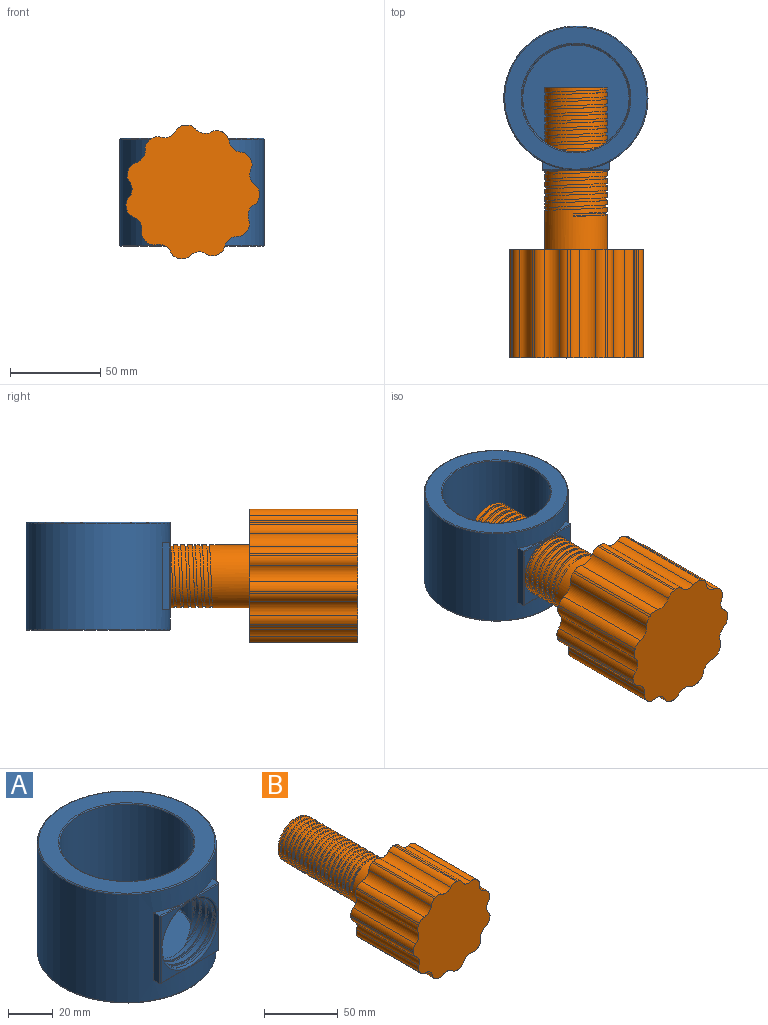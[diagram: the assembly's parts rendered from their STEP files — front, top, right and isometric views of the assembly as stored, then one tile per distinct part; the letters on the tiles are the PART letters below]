
ASSEMBLY  parts=2 mates=1
PART A: 45 faces, bbox 86.7x86.7x60.1 mm
  f0: plane 36.14x18.64mm, normal (0,-1,0), area 141.5mm2, adj f1,f39,f40,f41,f42,f43,f44
  f1: bspline ~6.95x0.63mm, area 1.6mm2, adj f0,f2,f39
  f2: cylinder r=40mm len=80mm, axis (0,0,-1), area 13405.1mm2, adj f1,f3,f4,f5,f6,f10,f11,f12
  f3: plane 12.2x4.04mm, normal (0,0,-1), area 20.2mm2, adj f2,f13,f39
  f4: plane 12.2x4.04mm, normal (0,0,-1), area 20.2mm2, adj f2,f5,f43
  f5: plane 37x4.04mm, normal (1,0,0), area 149.3mm2, adj f2,f4,f6,f42
  f6: plane 12.2x4.04mm, normal (0,0,1), area 20.2mm2, adj f2,f5,f7
  f7: cylinder r=0.5mm len=12.2mm, axis (-1,0,0), area 9.4mm2, adj f6,f8,f10,f42
  f8: plane 36.14x18.64mm, normal (0,-1,0), area 141.5mm2, adj f7,f9,f10,f11,f40,f41,f42
  f9: cylinder r=0.5mm len=12.2mm, axis (-1,0,0), area 9.4mm2, adj f8,f11,f12,f40
  f10: bspline ~6.95x0.63mm, area 1.6mm2, adj f2,f7,f8
  f11: bspline ~6.95x0.63mm, area 1.6mm2, adj f2,f8,f9
  f12: plane 12.2x4.04mm, normal (0,0,1), area 20.2mm2, adj f2,f9,f13
  f13: plane 37x4.04mm, normal (-1,0,0), area 149.3mm2, adj f2,f3,f12,f40
  f14: torus R=39.5mm, axis (0,0,1), area 196.5mm2, adj f2,f15
  f15: plane 79x79mm, normal (0,0,1), area 1979.2mm2, adj f14,f16
  f16: torus R=30.5mm, axis (0,0,1), area 148.9mm2, adj f15,f17
  f17: cylinder r=30mm len=60mm, axis (0,0,1), area 8262.7mm2, adj f16,f18,f20,f21,f22,f23,f24,f25
  f18: bspline ~40.99x35.5mm, area 184.4mm2, adj f17,f19,f24,f26
  f19: plane 0.97x0.75mm, normal (0,0,1), area 0.5mm2, adj f18,f26,f41
  f20: cylinder r=17mm len=21.91mm, axis (0,-1,0), area 35mm2, adj f17,f21
  f21: bspline ~30.74x9.25mm, area 19mm2, adj f17,f20,f22
  f22: cylinder r=17.75mm len=30.4mm, axis (0,-1,0), area 47.6mm2, adj f17,f21,f23
  f23: bspline ~35.87x26.63mm, area 26.9mm2, adj f17,f22,f24
  f24: cylinder r=17mm len=34mm, axis (0,-1,0), area 665.8mm2, adj f17,f18,f23,f25,f41
  f25: bspline ~40.99x35.5mm, area 201.3mm2, adj f17,f24,f26,f41
  f26: cylinder r=17.75mm len=35.5mm, axis (0,-1,0), area 443.9mm2, adj f17,f18,f19,f25,f27,f41
  f27: bspline ~35.87x26.63mm, area 31.5mm2, adj f17,f26,f28
  f28: cylinder r=17mm len=30.79mm, axis (0,-1,0), area 76.4mm2, adj f17,f27,f29
  f29: bspline ~30.74x9.25mm, area 16.6mm2, adj f17,f28,f30
  f30: cylinder r=17.75mm len=21.82mm, axis (0,-1,0), area 27.5mm2, adj f17,f29,f32
  f31: cylinder r=17mm len=7.73mm, axis (0,-1,0), area 0mm2, adj f17,f32
  f32: bspline ~30.74x9.25mm, area 7.8mm2, adj f17,f30,f31
  f33: bspline ~30.74x9.25mm, area 0mm2, adj f17,f34
  f34: cylinder r=17.75mm len=8.04mm, axis (0,-1,0), area 0mm2, adj f17,f33
  f35: torus R=29.5mm, axis (0,0,1), area 147.1mm2, adj f17,f36
  f36: plane 59x59mm, normal (0,0,1), area 2734mm2, adj f35
  f37: torus R=39.5mm, axis (0,0,1), area 196.5mm2, adj f2,f38
  f38: plane 79x79mm, normal (0,0,-1), area 4901.7mm2, adj f37
  f39: cylinder r=0.5mm len=12.2mm, axis (1,0,0), area 9.4mm2, adj f0,f1,f3,f40
  f40: cylinder r=0.5mm len=37mm, axis (0,0,-1), area 28.7mm2, adj f0,f8,f9,f13,f39
  f41: torus R=18mm, axis (0,-1,0), area 138.2mm2, adj f0,f8,f19,f24,f25,f26
  f42: cylinder r=0.5mm len=37mm, axis (0,0,1), area 28.7mm2, adj f0,f5,f7,f8,f43
  f43: cylinder r=0.5mm len=12.2mm, axis (1,0,0), area 9.4mm2, adj f0,f4,f42,f44
  f44: bspline ~6.95x0.63mm, area 1.6mm2, adj f0,f2,f43
PART B: 76 faces, bbox 73.9x150x74.3 mm
  f0: cylinder r=37.43mm len=60mm, axis (0,-1,0), area 76.3mm2, adj f1,f41,f72,f74
  f1: cylinder r=6mm len=60mm, axis (0,1,0), area 347.5mm2, adj f0,f3,f41,f72
  f2: cylinder r=6mm len=60mm, axis (0,1,0), area 347.5mm2, adj f3,f4,f41,f72
  f3: cylinder r=7mm len=60mm, axis (0,-1,0), area 585.2mm2, adj f1,f2,f41,f72
  f4: cylinder r=37.43mm len=60mm, axis (0,-1,0), area 76.3mm2, adj f2,f5,f41,f72
  f5: cylinder r=6mm len=60mm, axis (0,1,0), area 347.5mm2, adj f4,f7,f41,f72
  f6: cylinder r=6mm len=60mm, axis (0,1,0), area 347.5mm2, adj f7,f8,f41,f72
  f7: cylinder r=7mm len=60mm, axis (0,-1,0), area 585.2mm2, adj f5,f6,f41,f72
  f8: cylinder r=37.43mm len=60mm, axis (0,-1,0), area 76.3mm2, adj f6,f9,f41,f72
  f9: cylinder r=6mm len=60mm, axis (0,1,0), area 347.5mm2, adj f8,f11,f41,f72
  f10: cylinder r=6mm len=60mm, axis (0,1,0), area 347.5mm2, adj f11,f12,f41,f72
  f11: cylinder r=7mm len=60mm, axis (0,-1,0), area 585.2mm2, adj f9,f10,f41,f72
  f12: cylinder r=37.43mm len=60mm, axis (0,-1,0), area 76.3mm2, adj f10,f13,f41,f72
  f13: cylinder r=6mm len=60mm, axis (0,1,0), area 347.5mm2, adj f12,f15,f41,f72
  f14: cylinder r=6mm len=60mm, axis (0,1,0), area 347.5mm2, adj f15,f16,f41,f72
  f15: cylinder r=7mm len=60mm, axis (0,-1,0), area 585.2mm2, adj f13,f14,f41,f72
  f16: cylinder r=37.43mm len=60mm, axis (0,-1,0), area 76.3mm2, adj f14,f17,f41,f72
  f17: cylinder r=6mm len=60mm, axis (0,1,0), area 347.5mm2, adj f16,f19,f41,f72
  f18: cylinder r=6mm len=60mm, axis (0,1,0), area 347.5mm2, adj f19,f20,f41,f72
  f19: cylinder r=7mm len=60mm, axis (0,-1,0), area 585.2mm2, adj f17,f18,f41,f72
  f20: cylinder r=37.43mm len=60mm, axis (0,-1,0), area 76.3mm2, adj f18,f21,f41,f72
  f21: cylinder r=6mm len=60mm, axis (0,1,0), area 347.5mm2, adj f20,f23,f41,f72
  f22: cylinder r=6mm len=60mm, axis (0,1,0), area 347.5mm2, adj f23,f24,f41,f72
  f23: cylinder r=7mm len=60mm, axis (0,-1,0), area 585.2mm2, adj f21,f22,f41,f72
  f24: cylinder r=37.43mm len=60mm, axis (0,-1,0), area 76.3mm2, adj f22,f25,f41,f72
  f25: cylinder r=6mm len=60mm, axis (0,1,0), area 347.5mm2, adj f24,f27,f41,f72
  f26: cylinder r=6mm len=60mm, axis (0,1,0), area 347.5mm2, adj f27,f28,f41,f72
  f27: cylinder r=7mm len=60mm, axis (0,-1,0), area 585.2mm2, adj f25,f26,f41,f72
  f28: cylinder r=37.43mm len=60mm, axis (0,-1,0), area 76.3mm2, adj f26,f29,f41,f72
  f29: cylinder r=6mm len=60mm, axis (0,1,0), area 347.5mm2, adj f28,f31,f41,f72
  f30: cylinder r=6mm len=60mm, axis (0,1,0), area 347.5mm2, adj f31,f32,f41,f72
  f31: cylinder r=7mm len=60mm, axis (0,-1,0), area 585.2mm2, adj f29,f30,f41,f72
  f32: cylinder r=37.43mm len=60mm, axis (0,-1,0), area 76.3mm2, adj f30,f33,f41,f72
  f33: cylinder r=6mm len=60mm, axis (0,1,0), area 347.5mm2, adj f32,f35,f41,f72
  f34: cylinder r=6mm len=60mm, axis (0,1,0), area 347.5mm2, adj f35,f36,f41,f72
  f35: cylinder r=7mm len=60mm, axis (0,-1,0), area 585.2mm2, adj f33,f34,f41,f72
  f36: cylinder r=37.43mm len=60mm, axis (0,-1,0), area 76.3mm2, adj f34,f37,f41,f72
  f37: cylinder r=6mm len=60mm, axis (0,1,0), area 347.5mm2, adj f36,f39,f41,f72
  f38: cylinder r=6mm len=60mm, axis (0,1,0), area 347.5mm2, adj f39,f40,f41,f72
  f39: cylinder r=7mm len=60mm, axis (0,-1,0), area 585.2mm2, adj f37,f38,f41,f72
  f40: cylinder r=37.43mm len=60mm, axis (0,-1,0), area 76.3mm2, adj f38,f41,f72,f75
  f41: plane 74.35x73.91mm, normal (0,1,0), area 3007.2mm2, adj f0,f1,f2,f3,f4,f5,f6,f7
  f42: plane 34.02x33.7mm, normal (0,-1,0), area 90.4mm2, adj f44,f45,f48,f49,f50
  f43: plane 34.02x34.02mm, normal (0,1,0), area 99mm2, adj f44,f45,f48,f49,f51
  f44: cylinder r=17.01mm len=34.02mm, axis (0,1,0), area 78.7mm2, adj f42,f43,f48,f49
  f45: cylinder r=16.01mm len=32.02mm, axis (0,1,0), area 100.6mm2, adj f42,f43
  f46: plane 1.56x0.76mm, normal (0,0,1), area 1.2mm2, adj f49,f50,f53,f71
  f47: bspline ~70x40.38mm, area 1434.8mm2, adj f48,f50,f52,f53,f54,f55,f56,f57
  f48: plane 1.6x0.76mm, normal (0,0,1), area 0.9mm2, adj f42,f43,f44,f47,f49,f50,f51,f52
  f49: bspline ~70x40.38mm, area 1425.4mm2, adj f42,f43,f44,f46,f48,f50,f51,f52
  f50: cylinder r=16.69mm len=70mm, axis (0,-1,0), area 2782.5mm2, adj f42,f46,f47,f48,f49,f71
  f51: cylinder r=16.69mm len=12.69mm, axis (0,-1,0), area 4mm2, adj f43,f48,f49
  f52: cylinder r=17.45mm len=34.9mm, axis (0,1,0), area 2307.3mm2, adj f41,f47,f48,f49,f69
  f53: cylinder r=17.45mm len=34.9mm, axis (0,1,0), area 267.8mm2, adj f46,f47,f49,f54,f70,f71
  f54: cylinder r=17.45mm len=34.9mm, axis (0,1,0), area 263.2mm2, adj f47,f49,f53,f55
  f55: cylinder r=17.45mm len=34.9mm, axis (0,1,0), area 263.2mm2, adj f47,f49,f54,f56
  f56: cylinder r=17.45mm len=34.9mm, axis (0,1,0), area 263.1mm2, adj f47,f49,f55,f57
  f57: cylinder r=17.45mm len=34.9mm, axis (0,1,0), area 263.1mm2, adj f47,f49,f56,f58
  f58: cylinder r=17.45mm len=34.9mm, axis (0,1,0), area 263.1mm2, adj f47,f49,f57,f59
  f59: cylinder r=17.45mm len=34.9mm, axis (0,1,0), area 263.1mm2, adj f47,f49,f58,f60
  f60: cylinder r=17.45mm len=34.9mm, axis (0,1,0), area 263.1mm2, adj f47,f49,f59,f61
  f61: cylinder r=17.45mm len=34.9mm, axis (0,1,0), area 263.2mm2, adj f47,f49,f60,f62
  f62: cylinder r=17.45mm len=34.9mm, axis (0,1,0), area 263.2mm2, adj f47,f49,f61,f63
  f63: cylinder r=17.45mm len=34.9mm, axis (0,1,0), area 263.1mm2, adj f47,f49,f62,f64
  f64: cylinder r=17.45mm len=34.9mm, axis (0,1,0), area 263.1mm2, adj f47,f49,f63,f65
  f65: cylinder r=17.45mm len=34.9mm, axis (0,1,0), area 263.1mm2, adj f47,f49,f64,f66
  f66: cylinder r=17.45mm len=34.9mm, axis (0,1,0), area 263.1mm2, adj f47,f49,f65,f67
  f67: cylinder r=17.45mm len=34.9mm, axis (0,1,0), area 263.1mm2, adj f47,f49,f66,f68
  f68: cylinder r=17.45mm len=34.9mm, axis (0,1,0), area 263.1mm2, adj f47,f49,f67,f69
  f69: cylinder r=17.45mm len=34.9mm, axis (0,1,0), area 263.2mm2, adj f47,f49,f52,f68
  f70: cylinder r=17.45mm len=17.4mm, axis (0,1,0), area 12.5mm2, adj f47,f53,f71
  f71: plane 34.9x34.9mm, normal (0,1,0), area 955.7mm2, adj f46,f47,f50,f53,f70
  f72: plane 74.35x73.91mm, normal (0,-1,0), area 3963.8mm2, adj f0,f1,f2,f3,f4,f5,f6,f7
  f73: cylinder r=7mm len=60mm, axis (0,-1,0), area 585.2mm2, adj f41,f72,f74,f75
  f74: cylinder r=6mm len=60mm, axis (0,1,0), area 347.5mm2, adj f0,f41,f72,f73
  f75: cylinder r=6mm len=60mm, axis (0,1,0), area 347.5mm2, adj f40,f41,f72,f73
PLACE A t=(6.37,0,4.83)mm fixed
PLACE B rot(axis=(0,1,0),85.4deg) t=(6.37,5.84,34.83)mm
MATE cylindrical A.f20 <-> B.f0  axis (0,-1,0) through (6.37,-40,34.83)mm
